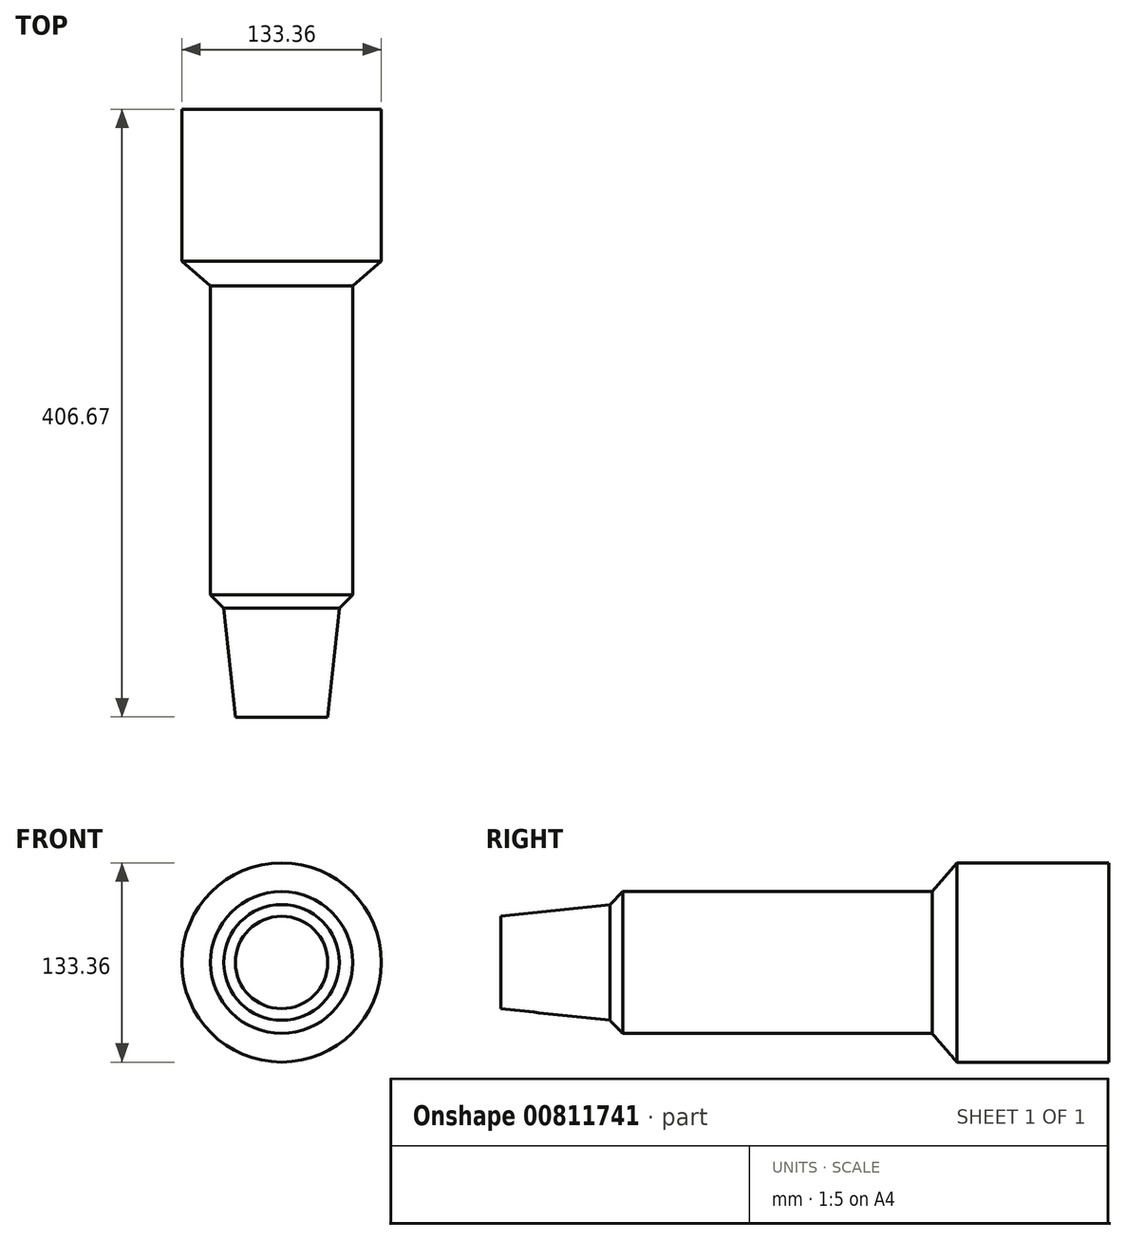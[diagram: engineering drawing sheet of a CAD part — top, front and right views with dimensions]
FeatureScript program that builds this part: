
annotation { "Feature Type Name" : "Feature", "Feature Type Description" : "" }
export const myFeature = defineFeature(function(context is Context, id is Id, definition is map)
    precondition{}
    {
        {
            var Q0;
            Q0=qCreatedBy(makeId("Right.planeOp"),FACE);
            var sketch = newSketch(context, id + "F0", { "sketchPlane" : qUnion([Q0])});
            skLineSegment(sketch, "E0", {"start": v(-209.49, 0) * mm, "end": v(196.91, 0) * mm});
            skLineSegment(sketch, "E1", {"start": v(196.91, 66.68) * mm, "end": v(196.91, 0) * mm});
            skLineSegment(sketch, "E2", {"start": v(196.91, 66.68) * mm, "end": v(95.31, 66.68) * mm});
            skLineSegment(sketch, "E3", {"start": v(95.31, 66.68) * mm, "end": v(78.77, 47.5) * mm});
            skLineSegment(sketch, "E4", {"start": v(78.77, 47.5) * mm, "end": v(-128.16, 47.5) * mm});
            skLineSegment(sketch, "E5", {"start": v(-128.16, 47.5) * mm, "end": v(-136.9, 38.7) * mm});
            skLineSegment(sketch, "E6", {"start": v(-136.9, 38.7) * mm, "end": v(-209.76, 30.93) * mm});
            skLineSegment(sketch, "E7", {"start": v(-209.76, 30.93) * mm, "end": v(-209.49, 0) * mm});
            skSolve(sketch);
        }
        {
            var Q0;
            Q0=makeQuery(id+"F0.imprint","IMPRINT",FACE,{"disambiguationData":[TD([[makeQuery(id+"F0.imprint","IMPRINT",EDGE,{"derivedFrom":sQuery(id+"F0.wireOp",EDGE,"E0")}),1.0]])]});
            var Q1;
            Q1=sQuery(id+"F0.wireOp",EDGE,"E0");
            revolve(context, id + "F1", {"surfaceOperationType" : NewSurfaceOperationType.NEW, "entities" : qUnion([Q0]), "axis" : qUnion([Q1]), "revolveType" : RevolveType.FULL});
        }
    });
